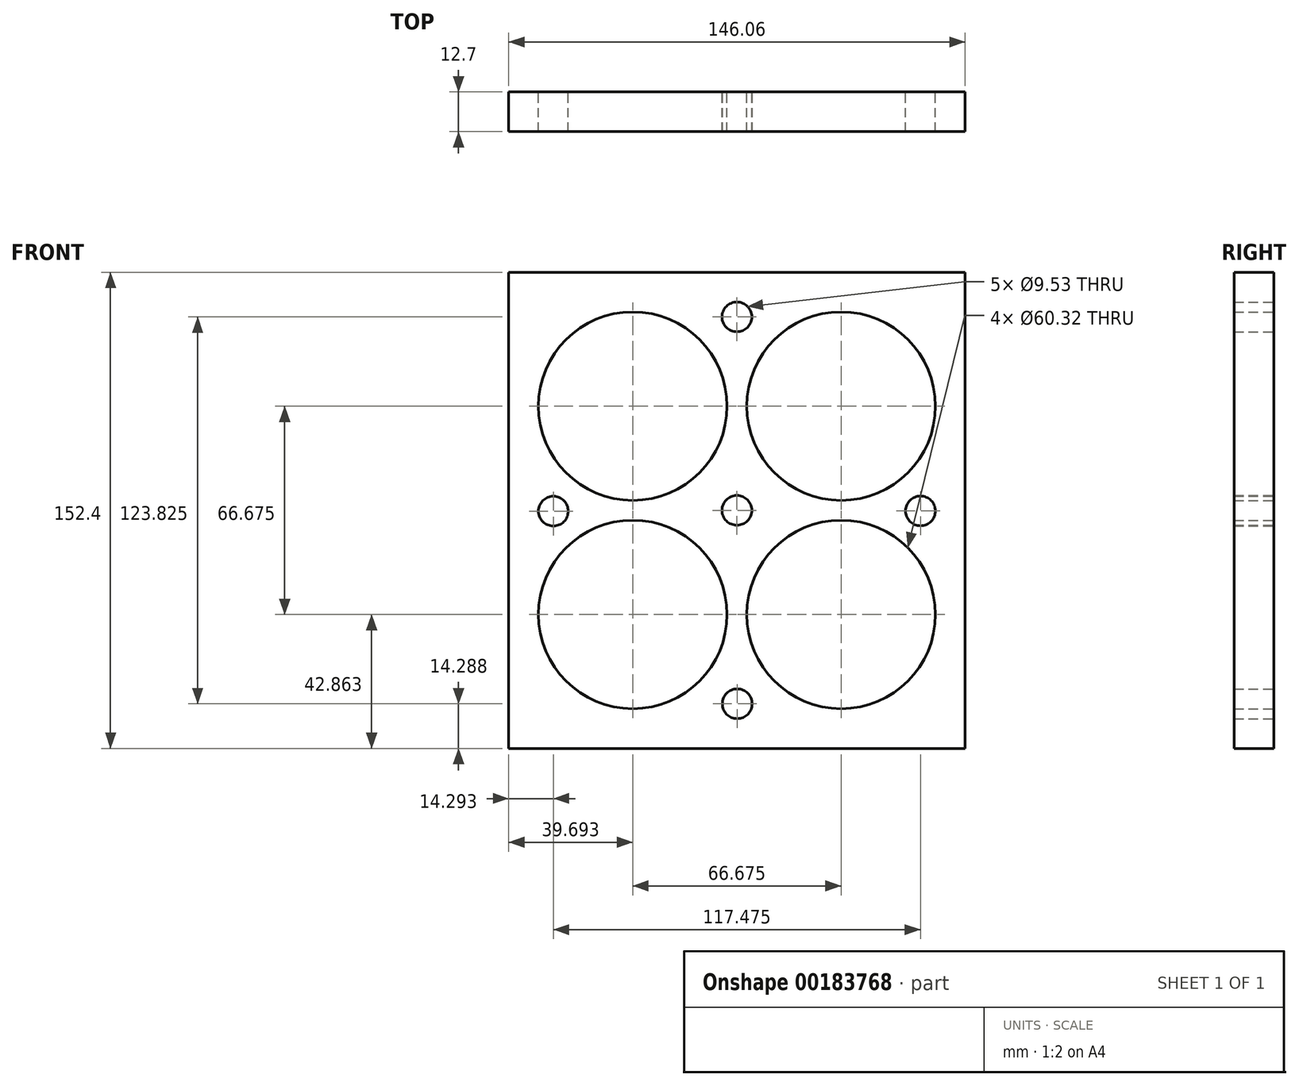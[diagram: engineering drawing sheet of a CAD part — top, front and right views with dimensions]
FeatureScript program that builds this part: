
annotation { "Feature Type Name" : "Feature", "Feature Type Description" : "" }
export const myFeature = defineFeature(function(context is Context, id is Id, definition is map)
    precondition{}
    {
        {
            var Q0;
            Q0=qCreatedBy(makeId("Front.planeOp"),FACE);
            var sketch = newSketch(context, id + "F0", { "sketchPlane" : qUnion([Q0])});
            skLineSegment(sketch, "E0.bottom", {"start": v(73.03, -76.2) * mm, "end": v(-73.02, -76.2) * mm});
            skLineSegment(sketch, "E0.top", {"start": v(73.02, 76.2) * mm, "end": v(-73.03, 76.2) * mm});
            skLineSegment(sketch, "E0.left", {"start": v(73.03, -76.2) * mm, "end": v(73.02, 76.2) * mm});
            skLineSegment(sketch, "E0.right", {"start": v(-73.02, -76.2) * mm, "end": v(-73.03, 76.2) * mm});
            skPoint(sketch, "E0.middle", {"position": v(0, 0) * mm});
            skCircle(sketch, "E1", {"center": v(-33.34, 33.34) * mm, "radius": 30.16 * mm});
            skCircle(sketch, "E2", {"center": v(33.34, 33.34) * mm, "radius": 30.16 * mm});
            skCircle(sketch, "E3", {"center": v(33.34, -33.34) * mm, "radius": 30.16 * mm});
            skCircle(sketch, "E4", {"center": v(-33.34, -33.34) * mm, "radius": 30.16 * mm});
            skCircle(sketch, "E5", {"center": v(0, 61.91) * mm, "radius": 4.76 * mm});
            skCircle(sketch, "E6", {"center": v(58.74, -0.2) * mm, "radius": 4.76 * mm});
            skCircle(sketch, "E7", {"center": v(0.1, -61.91) * mm, "radius": 4.76 * mm});
            skCircle(sketch, "E8", {"center": v(-58.74, -0.25) * mm, "radius": 4.76 * mm});
            skCircle(sketch, "E9", {"center": v(0, 0) * mm, "radius": 4.76 * mm});
            skSolve(sketch);
        }
        {
            var Q0;
            Q0=makeQuery(id+"F0.imprint","IMPRINT",FACE,{"disambiguationData":[TD([[makeQuery(id+"F0.imprint","IMPRINT",EDGE,{"derivedFrom":sQuery(id+"F0.wireOp",EDGE,"E0.bottom")}),-1.0]])]});
            extrude(context, id + "F1", {"entities" : qUnion([Q0]), "endBound" : BoundingType.SYMMETRIC, "depth" : 12.7 * mm});
        }
    });
